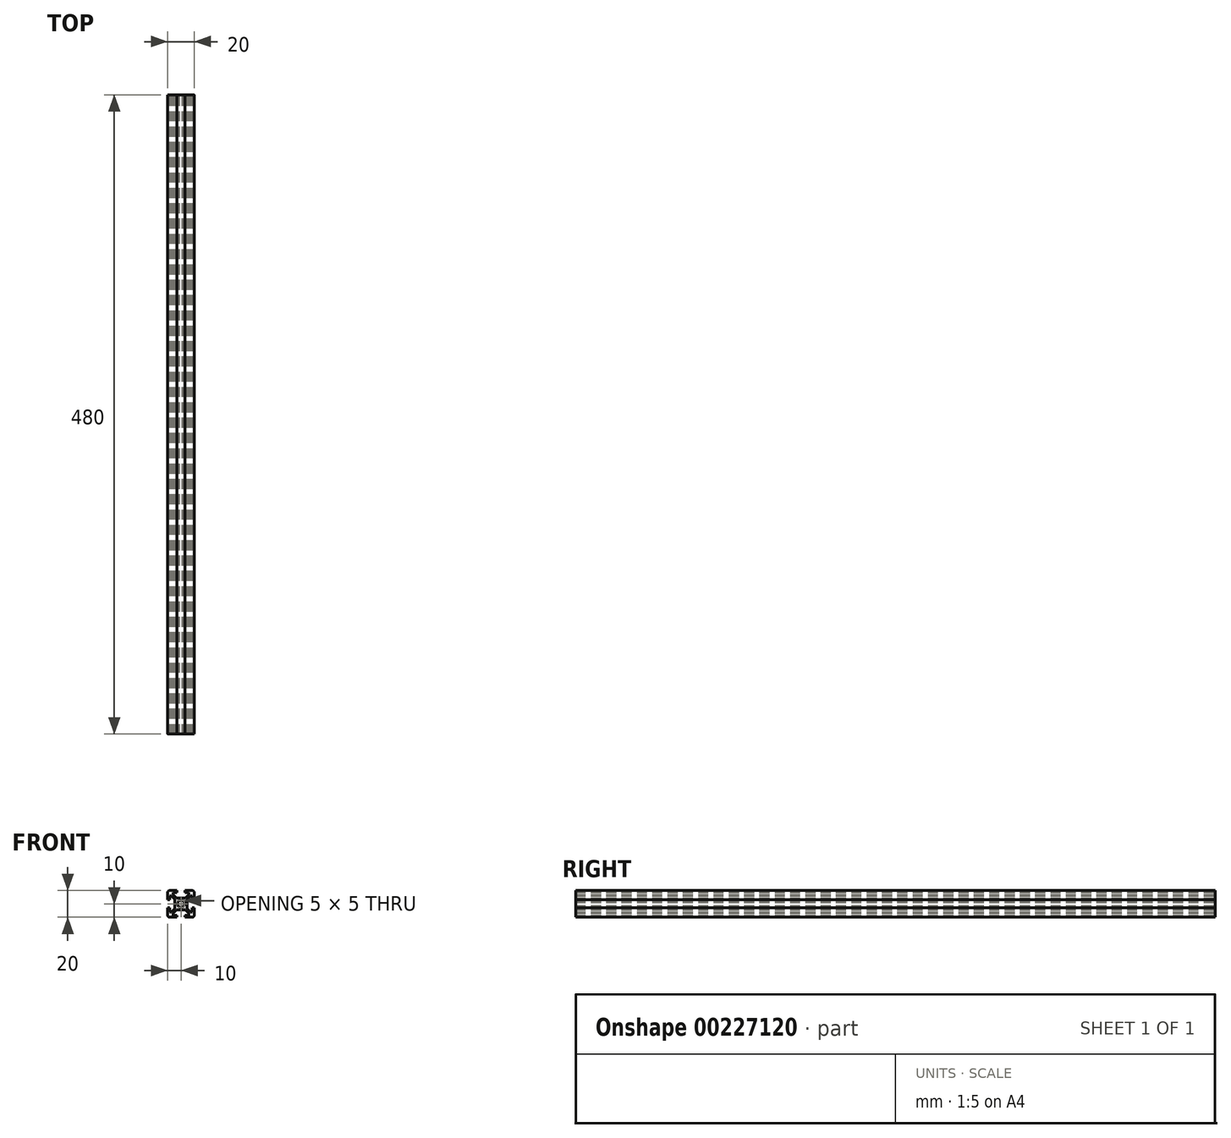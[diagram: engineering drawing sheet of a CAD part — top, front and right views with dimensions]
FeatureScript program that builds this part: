
annotation { "Feature Type Name" : "Feature", "Feature Type Description" : "" }
export const myFeature = defineFeature(function(context is Context, id is Id, definition is map)
    precondition{}
    {
        {
            var Q0;
            Q0=qCreatedBy(makeId("Front.planeOp"),FACE);
            var sketch = newSketch(context, id + "F0", { "sketchPlane" : qUnion([Q0])});
            skLineSegment(sketch, "E0.bottom", {"start": v(8.5, -10) * mm, "end": v(3, -10) * mm});
            skLineSegment(sketch, "E0.top", {"start": v(8.5, 10) * mm, "end": v(3, 10) * mm});
            skLineSegment(sketch, "E0.left", {"start": v(10, -8.5) * mm, "end": v(10, -3) * mm});
            skLineSegment(sketch, "E0.right", {"start": v(-10, -8.5) * mm, "end": v(-10, -3) * mm});
            skPoint(sketch, "E0.middle", {"position": v(0, 0) * mm});
            skLineSegment(sketch, "E1.bottom", {"start": v(6, -8.5) * mm, "end": v(3, -8.5) * mm});
            skLineSegment(sketch, "E1.top", {"start": v(6, 8.5) * mm, "end": v(3, 8.5) * mm});
            skLineSegment(sketch, "E1.left", {"start": v(8.5, -6) * mm, "end": v(8.5, -3) * mm});
            skLineSegment(sketch, "E1.right", {"start": v(-8.5, -6) * mm, "end": v(-8.5, -3) * mm});
            skLineSegment(sketch, "E2.bottom", {"start": v(3.44, -4.5) * mm, "end": v(-3.44, -4.5) * mm});
            skLineSegment(sketch, "E2.top", {"start": v(3.44, 4.5) * mm, "end": v(-3.44, 4.5) * mm});
            skLineSegment(sketch, "E2.left", {"start": v(4.5, -3.44) * mm, "end": v(4.5, 3.44) * mm});
            skLineSegment(sketch, "E2.right", {"start": v(-4.5, -3.44) * mm, "end": v(-4.5, 3.44) * mm});
            skLineSegment(sketch, "E3.bottom", {"start": v(8.5, -6) * mm, "end": v(7.06, -6) * mm});
            skLineSegment(sketch, "E3.top", {"start": v(8.5, 6) * mm, "end": v(7.06, 6) * mm});
            skLineSegment(sketch, "E4.left", {"start": v(6, -8.5) * mm, "end": v(6, -7.06) * mm});
            skLineSegment(sketch, "E4.right", {"start": v(-6, -8.5) * mm, "end": v(-6, -7.06) * mm});
            skPoint(sketch, "E5.orphan", {"position": v(-8.5, 8.5) * mm});
            skPoint(sketch, "E6.orphan", {"position": v(8.5, 8.5) * mm});
            skPoint(sketch, "E7.orphan", {"position": v(8.5, -8.5) * mm});
            skPoint(sketch, "E8.orphan", {"position": v(-8.5, -8.5) * mm});
            skLineSegment(sketch, "E9.trimOffspring", {"start": v(-6, 7.06) * mm, "end": v(-6, 8.5) * mm});
            skLineSegment(sketch, "E10.trimOffspring", {"start": v(-7.06, 6) * mm, "end": v(-8.5, 6) * mm});
            skLineSegment(sketch, "E11.trimOffspring", {"start": v(6, 7.06) * mm, "end": v(6, 8.5) * mm});
            skLineSegment(sketch, "E12.trimOffspring", {"start": v(-7.06, -6) * mm, "end": v(-8.5, -6) * mm});
            skLineSegment(sketch, "E13", {"start": v(-10, 10) * mm, "end": v(0, 0) * mm, "construction": true});
            skLineSegment(sketch, "E14", {"start": v(10, 10) * mm, "end": v(0, 0) * mm, "construction": true});
            skLineSegment(sketch, "E15", {"start": v(-6, 7.06) * mm, "end": v(-3.44, 4.5) * mm});
            skPoint(sketch, "E15.endSnap0", {"position": v(7.25, -6) * mm});
            skLineSegment(sketch, "E16", {"start": v(6, -7.06) * mm, "end": v(3.44, -4.5) * mm});
            skLineSegment(sketch, "E17", {"start": v(7.06, 6) * mm, "end": v(4.5, 3.44) * mm});
            skLineSegment(sketch, "E18", {"start": v(6, 7.06) * mm, "end": v(3.44, 4.5) * mm});
            skPoint(sketch, "E19.orphan", {"position": v(6, -6) * mm});
            skPoint(sketch, "E20.orphan", {"position": v(-4.5, -4.5) * mm});
            skPoint(sketch, "E21.orphan", {"position": v(-4.5, 4.5) * mm});
            skPoint(sketch, "E22.orphan", {"position": v(4.5, 4.5) * mm});
            skPoint(sketch, "E23.orphan", {"position": v(4.5, -4.5) * mm});
            skLineSegment(sketch, "E24.trimOffspring", {"start": v(4.5, -3.44) * mm, "end": v(7.06, -6) * mm});
            skLineSegment(sketch, "E25.trimOffspring", {"start": v(-3.44, -4.5) * mm, "end": v(-6, -7.06) * mm});
            skLineSegment(sketch, "E26.trimOffspring", {"start": v(-4.5, -3.44) * mm, "end": v(-7.06, -6) * mm});
            skLineSegment(sketch, "E27.trimOffspring", {"start": v(-4.5, 3.44) * mm, "end": v(-7.06, 6) * mm});
            skLineSegment(sketch, "E28.bottom", {"start": v(8.5, -3) * mm, "end": v(10, -3) * mm});
            skLineSegment(sketch, "E28.top", {"start": v(8.5, 3) * mm, "end": v(10, 3) * mm});
            skPoint(sketch, "E28.middle", {"position": v(10, 0) * mm});
            skLineSegment(sketch, "E29.left", {"start": v(3, 8.5) * mm, "end": v(3, 10) * mm});
            skLineSegment(sketch, "E29.right", {"start": v(-3, 8.5) * mm, "end": v(-3, 10) * mm});
            skPoint(sketch, "E29.middle", {"position": v(0, 10) * mm});
            skLineSegment(sketch, "E30.bottom", {"start": v(-8.5, 3) * mm, "end": v(-10, 3) * mm});
            skLineSegment(sketch, "E30.top", {"start": v(-8.5, -3) * mm, "end": v(-10, -3) * mm});
            skPoint(sketch, "E30.middle", {"position": v(-10, 0) * mm});
            skLineSegment(sketch, "E31.left", {"start": v(3, -8.5) * mm, "end": v(3, -10) * mm});
            skLineSegment(sketch, "E31.right", {"start": v(-3, -8.5) * mm, "end": v(-3, -10) * mm});
            skPoint(sketch, "E31.middle", {"position": v(0, -10) * mm});
            skPoint(sketch, "E32.orphan", {"position": v(3, 11.5) * mm});
            skPoint(sketch, "E33.orphan", {"position": v(-3, 11.5) * mm});
            skLineSegment(sketch, "E34.trimOffspring", {"start": v(-3, 10) * mm, "end": v(-8.5, 10) * mm});
            skLineSegment(sketch, "E35.trimOffspring", {"start": v(-3, 8.5) * mm, "end": v(-6, 8.5) * mm});
            skPoint(sketch, "E28.right.end.orphan", {"position": v(11.5, 3) * mm});
            skPoint(sketch, "E36.orphan", {"position": v(11.5, -3) * mm});
            skLineSegment(sketch, "E37.trimOffspring", {"start": v(10, 3) * mm, "end": v(10, 8.5) * mm});
            skLineSegment(sketch, "E38.trimOffspring", {"start": v(8.5, 3) * mm, "end": v(8.5, 6) * mm});
            skPoint(sketch, "E39.orphan", {"position": v(3, -11.5) * mm});
            skPoint(sketch, "E40.orphan", {"position": v(-3, -11.5) * mm});
            skLineSegment(sketch, "E41.trimOffspring", {"start": v(-3, -10) * mm, "end": v(-8.5, -10) * mm});
            skLineSegment(sketch, "E42.trimOffspring", {"start": v(-3, -8.5) * mm, "end": v(-6, -8.5) * mm});
            skPoint(sketch, "E30.right.end.orphan", {"position": v(-11.5, -3) * mm});
            skPoint(sketch, "E43.orphan", {"position": v(-11.5, 3) * mm});
            skLineSegment(sketch, "E44.trimOffspring", {"start": v(-10, 3) * mm, "end": v(-10, 8.5) * mm});
            skLineSegment(sketch, "E45.trimOffspring", {"start": v(-8.5, 3) * mm, "end": v(-8.5, 6) * mm});
            skLineSegment(sketch, "E46.trimOffspring", {"start": v(0, 0) * mm, "end": v(10, -10) * mm, "construction": true});
            skLineSegment(sketch, "E47.trimOffspring", {"start": v(0, 0) * mm, "end": v(-10, -10) * mm, "construction": true});
            skArc(sketch, "E48", {"start": v(1.16, 2.22) * mm, "mid": v(0, 2.5) * mm, "end": v(-1.16, 2.22) * mm});
            skLineSegment(sketch, "E49", {"start": v(-2.5, -1.44) * mm, "end": v(1.44, 2.5) * mm});
            skLineSegment(sketch, "E50", {"start": v(2.5, 1.44) * mm, "end": v(-1.44, -2.5) * mm});
            skLineSegment(sketch, "E51", {"start": v(1.44, -2.5) * mm, "end": v(-2.5, 1.44) * mm});
            skLineSegment(sketch, "E52", {"start": v(-1.44, 2.5) * mm, "end": v(2.5, -1.44) * mm});
            skLineSegment(sketch, "E53", {"start": v(2.5, 1.44) * mm, "end": v(2.5, -1.44) * mm, "construction": true});
            skLineSegment(sketch, "E54", {"start": v(1.44, -2.5) * mm, "end": v(-1.44, -2.5) * mm, "construction": true});
            skLineSegment(sketch, "E55", {"start": v(-2.5, -1.44) * mm, "end": v(-2.5, 1.44) * mm, "construction": true});
            skLineSegment(sketch, "E56", {"start": v(-1.44, 2.5) * mm, "end": v(1.44, 2.5) * mm, "construction": true});
            skLineSegment(sketch, "E57", {"start": v(-1.44, 2.5) * mm, "end": v(-2.5, 1.44) * mm});
            skLineSegment(sketch, "E58", {"start": v(1.44, 2.5) * mm, "end": v(2.5, 1.44) * mm});
            skLineSegment(sketch, "E59", {"start": v(2.5, -1.44) * mm, "end": v(1.44, -2.5) * mm});
            skLineSegment(sketch, "E60", {"start": v(-1.44, -2.5) * mm, "end": v(-2.5, -1.44) * mm});
            skArc(sketch, "E61.trimOffspring", {"start": v(-2.22, 1.16) * mm, "mid": v(-2.5, 0) * mm, "end": v(-2.22, -1.16) * mm});
            skArc(sketch, "E62.trimOffspring", {"start": v(-1.16, -2.22) * mm, "mid": v(0, -2.5) * mm, "end": v(1.16, -2.22) * mm});
            skArc(sketch, "E63.trimOffspring", {"start": v(2.22, -1.16) * mm, "mid": v(2.5, 0) * mm, "end": v(2.22, 1.16) * mm});
            skPoint(sketch, "E64.visualSharp", {"position": v(10, 10) * mm});
            skArc(sketch, "E64.filletArc", {"start": v(10, 8.5) * mm, "mid": v(9.56, 9.56) * mm, "end": v(8.5, 10) * mm});
            skPoint(sketch, "E65.visualSharp", {"position": v(10, -10) * mm});
            skArc(sketch, "E65.filletArc", {"start": v(8.5, -10) * mm, "mid": v(9.56, -9.56) * mm, "end": v(10, -8.5) * mm});
            skPoint(sketch, "E66.visualSharp", {"position": v(-10, -10) * mm});
            skArc(sketch, "E66.filletArc", {"start": v(-10, -8.5) * mm, "mid": v(-9.56, -9.56) * mm, "end": v(-8.5, -10) * mm});
            skPoint(sketch, "E67.visualSharp", {"position": v(-10, 10) * mm});
            skArc(sketch, "E67.filletArc", {"start": v(-8.5, 10) * mm, "mid": v(-9.56, 9.56) * mm, "end": v(-10, 8.5) * mm});
            skSolve(sketch);
        }
        {
            assignVariable(context, id + "F2", {"name" : "Length", "anyValue" : 480});
        }
        {
            var Q0;
            Q0=qSketchRegion(id+"F0",true);
            extrude(context, id + "F1", {"entities" : qUnion([Q0]), "depth" : (getVariable(context, 'Length')) * mm});
        }
    });
